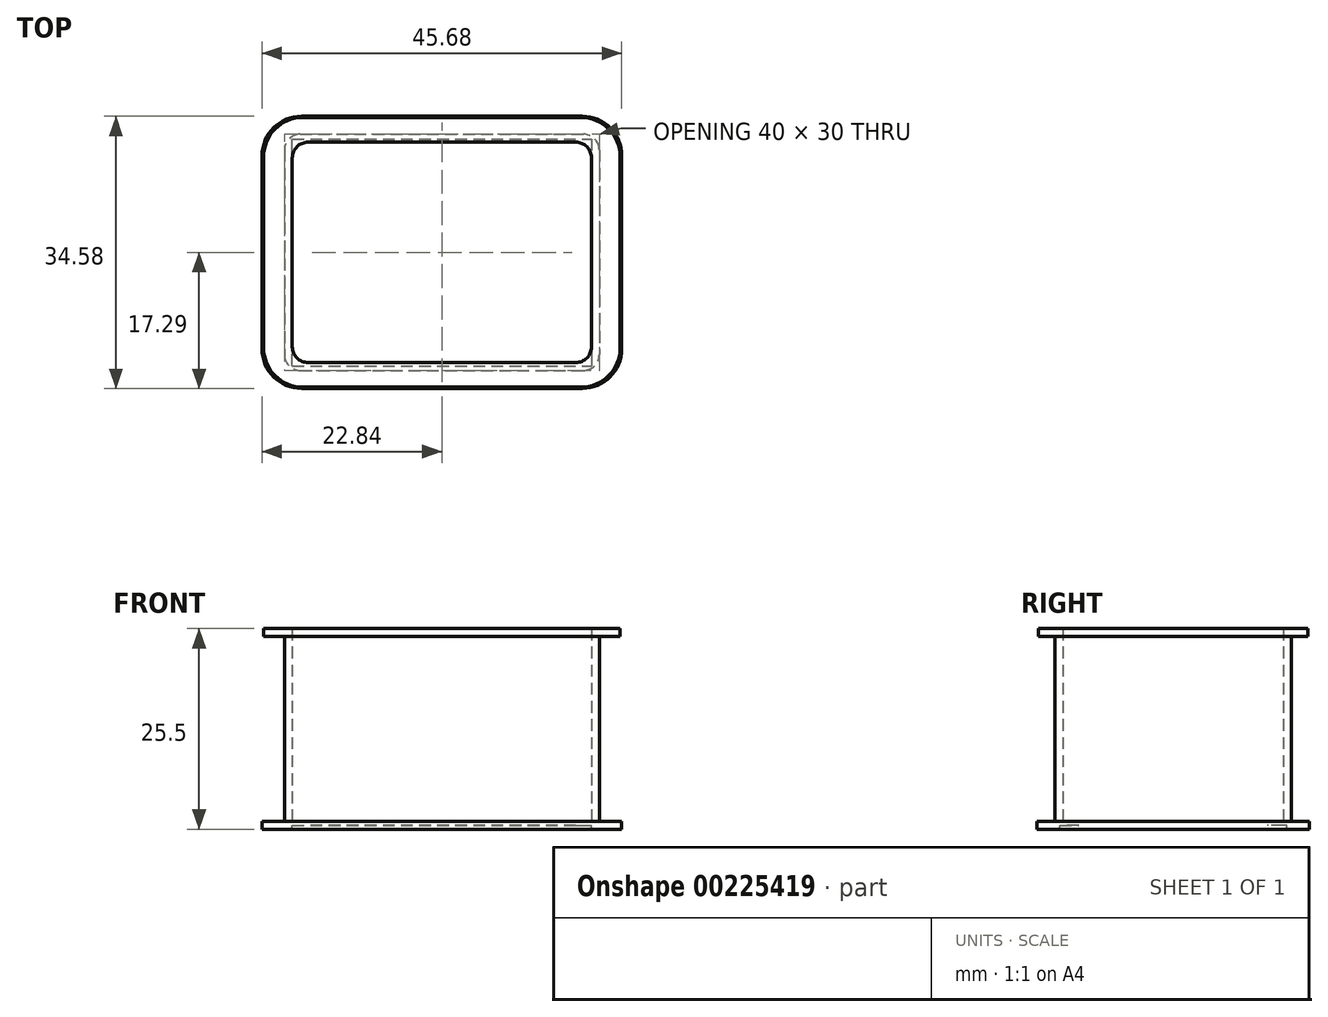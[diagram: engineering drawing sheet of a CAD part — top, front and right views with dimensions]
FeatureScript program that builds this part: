
annotation { "Feature Type Name" : "Feature", "Feature Type Description" : "" }
export const myFeature = defineFeature(function(context is Context, id is Id, definition is map)
    precondition{}
    {
        {
            var Q0;
            Q0=qCreatedBy(makeId("Top.planeOp"),FACE);
            var sketch = newSketch(context, id + "F0", { "sketchPlane" : qUnion([Q0])});
            skLineSegment(sketch, "E0.bottom", {"start": v(20, -15) * mm, "end": v(-20, -15) * mm});
            skLineSegment(sketch, "E0.top", {"start": v(20, 15) * mm, "end": v(-20, 15) * mm});
            skLineSegment(sketch, "E0.left", {"start": v(20, -15) * mm, "end": v(20, 15) * mm});
            skLineSegment(sketch, "E0.right", {"start": v(-20, -15) * mm, "end": v(-20, 15) * mm});
            skPoint(sketch, "E0.middle", {"position": v(0, 0) * mm});
            skLineSegment(sketch, "E1.0", {"start": v(19, 14) * mm, "end": v(-19, 14) * mm});
            skLineSegment(sketch, "E1.1", {"start": v(19, -14) * mm, "end": v(19, 14) * mm});
            skLineSegment(sketch, "E1.2", {"start": v(19, -14) * mm, "end": v(-19, -14) * mm});
            skLineSegment(sketch, "E1.3", {"start": v(-19, -14) * mm, "end": v(-19, 14) * mm});
            skSolve(sketch);
        }
        {
            var Q0;
            Q0 = qSketchRegion(id + "F0", true);
            extrude(context, id + "F1", {"entities" : qUnion([Q0]), "depth" : 25 * mm});
        }
        {
            var Q0;
            Q0=makeQuery(id+"F1.opExtrude","SWEPT_EDGE",EDGE,{"disambiguationData":[OSD([sQuery(id+"F0.wireOp",EDGE,"E1.2"),sQuery(id+"F0.wireOp",EDGE,"E1.3")])]});
            var Q1;
            Q1=makeQuery(id+"F1.opExtrude","SWEPT_EDGE",EDGE,{"disambiguationData":[OSD([sQuery(id+"F0.wireOp",EDGE,"E0.bottom"),sQuery(id+"F0.wireOp",EDGE,"E0.right")])]});
            var Q2;
            Q2=makeQuery(id+"F1.opExtrude","SWEPT_EDGE",EDGE,{"disambiguationData":[OSD([sQuery(id+"F0.wireOp",EDGE,"E0.top"),sQuery(id+"F0.wireOp",EDGE,"E0.right")])]});
            var Q3;
            Q3=makeQuery(id+"F1.opExtrude","SWEPT_EDGE",EDGE,{"disambiguationData":[OSD([sQuery(id+"F0.wireOp",EDGE,"E1.0"),sQuery(id+"F0.wireOp",EDGE,"E1.3")])]});
            var Q4;
            Q4=makeQuery(id+"F1.opExtrude","SWEPT_EDGE",EDGE,{"disambiguationData":[OSD([sQuery(id+"F0.wireOp",EDGE,"E1.1"),sQuery(id+"F0.wireOp",EDGE,"E1.2")])]});
            var Q5;
            Q5=makeQuery(id+"F1.opExtrude","SWEPT_EDGE",EDGE,{"disambiguationData":[OSD([sQuery(id+"F0.wireOp",EDGE,"E1.0"),sQuery(id+"F0.wireOp",EDGE,"E1.1")])]});
            var Q6;
            Q6=makeQuery(id+"F1.opExtrude","SWEPT_EDGE",EDGE,{"disambiguationData":[OSD([sQuery(id+"F0.wireOp",EDGE,"E0.top"),sQuery(id+"F0.wireOp",EDGE,"E0.left")])]});
            var Q7;
            Q7=makeQuery(id+"F1.opExtrude","SWEPT_EDGE",EDGE,{"disambiguationData":[OSD([sQuery(id+"F0.wireOp",EDGE,"E0.bottom"),sQuery(id+"F0.wireOp",EDGE,"E0.left")])]});
            fillet(context, id + "F2", {"entities" : qUnion([Q0, Q1, Q2, Q3, Q4, Q5, Q6, Q7]), "radius" : 2 * mm, "tangentPropagation" : true, "allowEdgeOverflow" : false});
        }
        {
            var Q0;
            Q0=makeQuery(id+"F1.opExtrude","CAP_FACE",FACE,{"disambiguationData":[OSD([sQuery(id+"F0.wireOp",EDGE,"E0.bottom"),sQuery(id+"F0.wireOp",EDGE,"E0.top"),sQuery(id+"F0.wireOp",EDGE,"E0.left"),sQuery(id+"F0.wireOp",EDGE,"E0.right"),sQuery(id+"F0.wireOp",EDGE,"E1.0"),sQuery(id+"F0.wireOp",EDGE,"E1.1"),sQuery(id+"F0.wireOp",EDGE,"E1.2"),sQuery(id+"F0.wireOp",EDGE,"E1.3")])],"isStart":false});
            var sketch = newSketch(context, id + "F3", { "sketchPlane" : qUnion([Q0])});
            skLineSegment(sketch, "E2.bottom", {"start": v(22.65, -17.14) * mm, "end": v(-22.65, -17.14) * mm});
            skLineSegment(sketch, "E2.top", {"start": v(22.65, 17.14) * mm, "end": v(-22.65, 17.14) * mm});
            skLineSegment(sketch, "E2.left", {"start": v(22.65, -17.14) * mm, "end": v(22.65, 17.14) * mm});
            skLineSegment(sketch, "E2.right", {"start": v(-22.65, -17.14) * mm, "end": v(-22.65, 17.14) * mm});
            skPoint(sketch, "E2.middle", {"position": v(0, 0) * mm});
            skLineSegment(sketch, "E3.bottom", {"start": v(19.41, -14.41) * mm, "end": v(-19.41, -14.41) * mm});
            skLineSegment(sketch, "E3.top", {"start": v(19.41, 14.41) * mm, "end": v(-19.41, 14.41) * mm});
            skLineSegment(sketch, "E3.left", {"start": v(19.41, -14.41) * mm, "end": v(19.41, 14.41) * mm});
            skLineSegment(sketch, "E3.right", {"start": v(-19.41, -14.41) * mm, "end": v(-19.41, 14.41) * mm});
            skSolve(sketch);
        }
        {
            var Q0;
            Q0 = qSketchRegion(id + "F3", true);
            extrude(context, id + "F4", {"entities" : qUnion([Q0]), "operationType" : NewBodyOperationType.ADD, "oppositeDirection" : true, "depth" : 1 * mm});
        }
        {
            var Q0;
            Q0=makeQuery(id+"F4.opExtrude","SWEPT_EDGE",EDGE,{"disambiguationData":[OSD([sQuery(id+"F3.wireOp",EDGE,"E2.top"),sQuery(id+"F3.wireOp",EDGE,"E2.right")])]});
            var Q1;
            Q1=makeQuery(id+"F4.opExtrude","SWEPT_EDGE",EDGE,{"disambiguationData":[OSD([sQuery(id+"F3.wireOp",EDGE,"E2.bottom"),sQuery(id+"F3.wireOp",EDGE,"E2.right")])]});
            var Q2;
            Q2=makeQuery(id+"F4.opExtrude","SWEPT_EDGE",EDGE,{"disambiguationData":[OSD([sQuery(id+"F3.wireOp",EDGE,"E2.top"),sQuery(id+"F3.wireOp",EDGE,"E2.left")])]});
            var Q3;
            Q3=makeQuery(id+"F4.opExtrude","SWEPT_EDGE",EDGE,{"disambiguationData":[OSD([sQuery(id+"F3.wireOp",EDGE,"E2.bottom"),sQuery(id+"F3.wireOp",EDGE,"E2.left")])]});
            fillet(context, id + "F5", {"entities" : qUnion([Q0, Q1, Q2, Q3]), "radius" : 5 * mm, "tangentPropagation" : true, "allowEdgeOverflow" : false});
        }
        {
            var Q0;
            Q0=makeQuery(id+"F1.opExtrude","CAP_FACE",FACE,{"disambiguationData":[OSD([sQuery(id+"F0.wireOp",EDGE,"E0.bottom"),sQuery(id+"F0.wireOp",EDGE,"E0.top"),sQuery(id+"F0.wireOp",EDGE,"E0.left"),sQuery(id+"F0.wireOp",EDGE,"E0.right"),sQuery(id+"F0.wireOp",EDGE,"E1.0"),sQuery(id+"F0.wireOp",EDGE,"E1.1"),sQuery(id+"F0.wireOp",EDGE,"E1.2"),sQuery(id+"F0.wireOp",EDGE,"E1.3")])],"isStart":true});
            var sketch = newSketch(context, id + "F6", { "sketchPlane" : qUnion([Q0])});
            skLineSegment(sketch, "E4.bottom", {"start": v(-22.84, -17.3) * mm, "end": v(22.84, -17.3) * mm});
            skLineSegment(sketch, "E4.top", {"start": v(-22.84, 17.3) * mm, "end": v(22.84, 17.3) * mm});
            skLineSegment(sketch, "E4.left", {"start": v(-22.84, -17.3) * mm, "end": v(-22.84, 17.3) * mm});
            skLineSegment(sketch, "E4.right", {"start": v(22.84, -17.3) * mm, "end": v(22.84, 17.3) * mm});
            skPoint(sketch, "E4.middle", {"position": v(0, 0) * mm});
            skLineSegment(sketch, "E5.bottom", {"start": v(-19, -14.41) * mm, "end": v(19, -14.41) * mm});
            skLineSegment(sketch, "E5.top", {"start": v(-19, 14.41) * mm, "end": v(19, 14.41) * mm});
            skLineSegment(sketch, "E5.left", {"start": v(-19, -14.41) * mm, "end": v(-19, 14.41) * mm});
            skLineSegment(sketch, "E5.right", {"start": v(19, -14.41) * mm, "end": v(19, 14.41) * mm});
            skPoint(sketch, "E5.cornerSnap0", {"position": v(-19.41, -14.41) * mm});
            skSolve(sketch);
        }
        {
            var Q0;
            Q0 = qSketchRegion(id + "F6", true);
            extrude(context, id + "F7", {"entities" : qUnion([Q0]), "operationType" : NewBodyOperationType.ADD, "endBound" : BoundingType.SYMMETRIC, "depth" : 1 * mm});
        }
        {
            var Q0;
            Q0=makeQuery(id+"F7.opExtrude","SWEPT_EDGE",EDGE,{"disambiguationData":[OSD([sQuery(id+"F6.wireOp",EDGE,"E4.top"),sQuery(id+"F6.wireOp",EDGE,"E4.left")])]});
            var Q1;
            Q1=makeQuery(id+"F7.opExtrude","SWEPT_EDGE",EDGE,{"disambiguationData":[OSD([sQuery(id+"F6.wireOp",EDGE,"E4.top"),sQuery(id+"F6.wireOp",EDGE,"E4.right")])]});
            var Q2;
            Q2=makeQuery(id+"F7.opExtrude","SWEPT_EDGE",EDGE,{"disambiguationData":[OSD([sQuery(id+"F6.wireOp",EDGE,"E4.bottom"),sQuery(id+"F6.wireOp",EDGE,"E4.left")])]});
            var Q3;
            Q3=makeQuery(id+"F7.opExtrude","SWEPT_EDGE",EDGE,{"disambiguationData":[OSD([sQuery(id+"F6.wireOp",EDGE,"E4.bottom"),sQuery(id+"F6.wireOp",EDGE,"E4.right")])]});
            fillet(context, id + "F8", {"entities" : qUnion([Q0, Q1, Q2, Q3]), "radius" : 5 * mm, "tangentPropagation" : true, "allowEdgeOverflow" : false});
        }
    });
